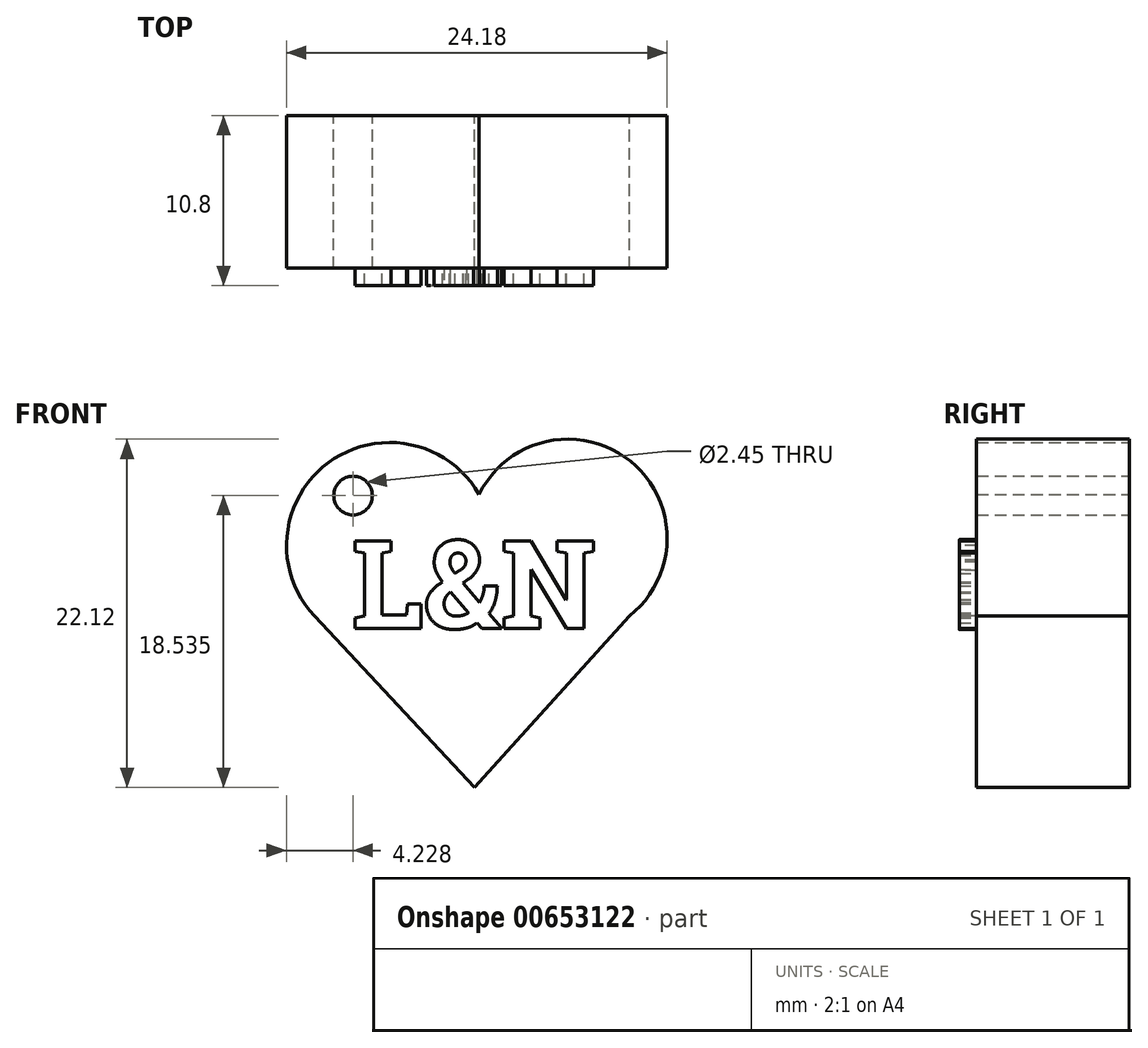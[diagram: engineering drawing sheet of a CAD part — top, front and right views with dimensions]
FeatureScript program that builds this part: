
annotation { "Feature Type Name" : "Feature", "Feature Type Description" : "" }
export const myFeature = defineFeature(function(context is Context, id is Id, definition is map)
    precondition{}
    {
        {
            var Q0;
            Q0=qCreatedBy(makeId("Front.planeOp"),FACE);
            var sketch = newSketch(context, id + "F0", { "sketchPlane" : qUnion([Q0])});
            skLineSegment(sketch, "E0", {"start": v(12.29, -4.86) * mm, "end": v(2.1, 6.02) * mm});
            skPoint(sketch, "E0.endSnap0", {"position": v(-3.18, 6.02) * mm});
            skLineSegment(sketch, "E1", {"start": v(12.29, -4.86) * mm, "end": v(22.1, 6.02) * mm});
            skArc(sketch, "E2", {"start": v(12.56, 13.75) * mm, "mid": v(3, 15.76) * mm, "end": v(2.1, 6.02) * mm});
            skArc(sketch, "E3", {"start": v(22.1, 6.02) * mm, "mid": v(22.18, 15.86) * mm, "end": v(12.56, 13.75) * mm});
            skSolve(sketch);
        }
        {
            var Q0;
            Q0 = qSketchRegion(id + "F0", true);
            extrude(context, id + "F1", {"entities" : qUnion([Q0]), "depth" : 9.7 * mm, "offsetDistance" : 25 * mm});
        }
        {
            var Q0;
            Q0=qCreatedBy(makeId("Front.planeOp"),FACE);
            var sketch = newSketch(context, id + "F2", { "sketchPlane" : qUnion([Q0])});
            skCircle(sketch, "E4", {"center": v(4.56, 13.67) * mm, "radius": 1.23 * mm});
            skSolve(sketch);
        }
        {
            var Q0;
            Q0 = qSketchRegion(id + "F2", true);
            extrude(context, id + "F3", {"entities" : qUnion([Q0]), "operationType" : NewBodyOperationType.REMOVE, "endBound" : BoundingType.UP_TO_NEXT, "depth" : 101 * mm, "offsetDistance" : 25 * mm});
        }
        {
            var Q0;
            Q0=qCreatedBy(makeId("Front.planeOp"),FACE);
            var sketch = newSketch(context, id + "F4", { "sketchPlane" : qUnion([Q0])});
            skText(sketch, "E5", { "text": "L&N", "fontName": "RobotoSlab-Bold.ttf"});
            const initialGuessF4  = {"E5": [0.00447, 0.00524, 1, 0, 0.00563]};
            skSetInitialGuess(sketch, initialGuessF4);
            skSolve(sketch);
        }
        {
            var Q0;
            Q0 = qSketchRegion(id + "F4", true);
            extrude(context, id + "F5", {"entities" : qUnion([Q0]), "operationType" : NewBodyOperationType.ADD, "depth" : 10.8 * mm, "offsetDistance" : 25 * mm});
        }
    });
